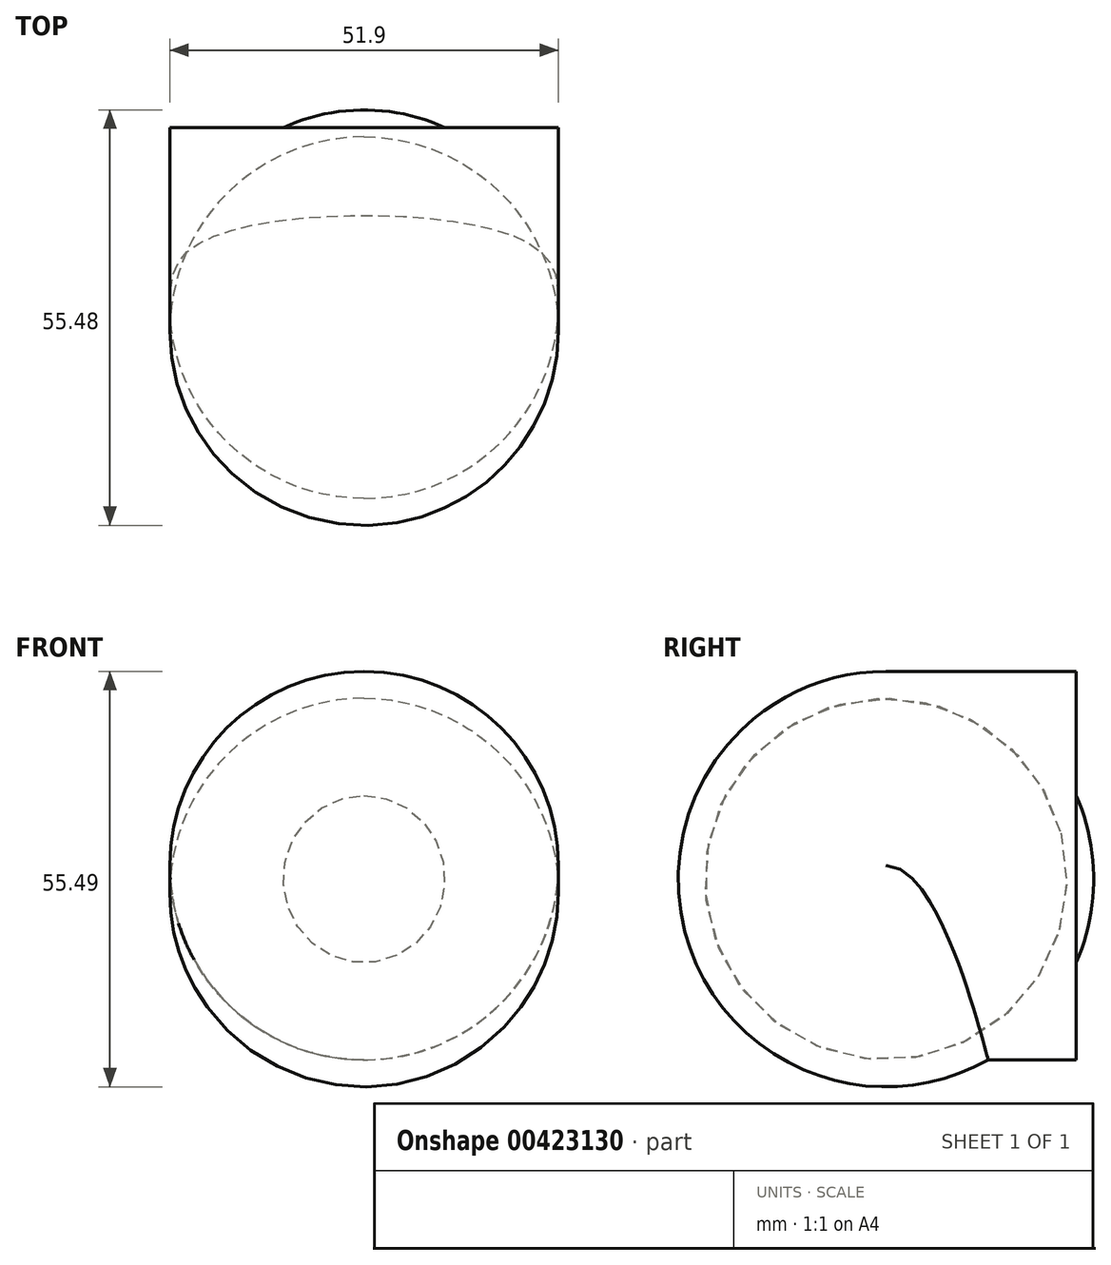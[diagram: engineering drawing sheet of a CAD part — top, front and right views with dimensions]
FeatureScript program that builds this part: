
annotation { "Feature Type Name" : "Feature", "Feature Type Description" : "" }
export const myFeature = defineFeature(function(context is Context, id is Id, definition is map)
    precondition{}
    {
        {
            var Q0;
            Q0=qCreatedBy(makeId("Front.planeOp"),FACE);
            var sketch = newSketch(context, id + "F0", { "sketchPlane" : qUnion([Q0])});
            skCircle(sketch, "E0", {"center": v(-35.6, 28.04) * mm, "radius": 25.95 * mm});
            skSolve(sketch);
        }
        {
            var Q0;
            Q0 = qSketchRegion(id + "F0", true);
            extrude(context, id + "F1", {"entities" : qUnion([Q0]), "depth" : 25.4 * mm});
        }
        {
            var Q0;
            Q0=makeQuery(id+"F1.opExtrude","CAP_FACE",FACE,{"disambiguationData":[OSD([sQuery(id+"F0.wireOp",EDGE,"E0")])],"isStart":false});
            var sketch = newSketch(context, id + "F2", { "sketchPlane" : qUnion([Q0])});
            skLineSegment(sketch, "E1", {"start": v(-61.5, 26.25) * mm, "end": v(-9.72, 26.25) * mm});
            skSolve(sketch);
        }
        {
            var Q0;
            {var subQ0=sQuery(id+"F2.wireOp",EDGE,"E1");Q0=makeQuery(id+"F2.imprint","IMPRINT",FACE,{"disambiguationData":[TD([[makeQuery(id+"F2.imprint","IMPRINT",EDGE,{"derivedFrom":subQ0}),1.0]])]});}
            var Q1;
            Q1=sQuery(id+"F2.wireOp",EDGE,"E1");
            revolve(context, id + "F3", {"operationType" : NewBodyOperationType.ADD, "entities" : qUnion([Q0]), "axis" : qUnion([Q1]), "revolveType" : RevolveType.FULL});
        }
    });
